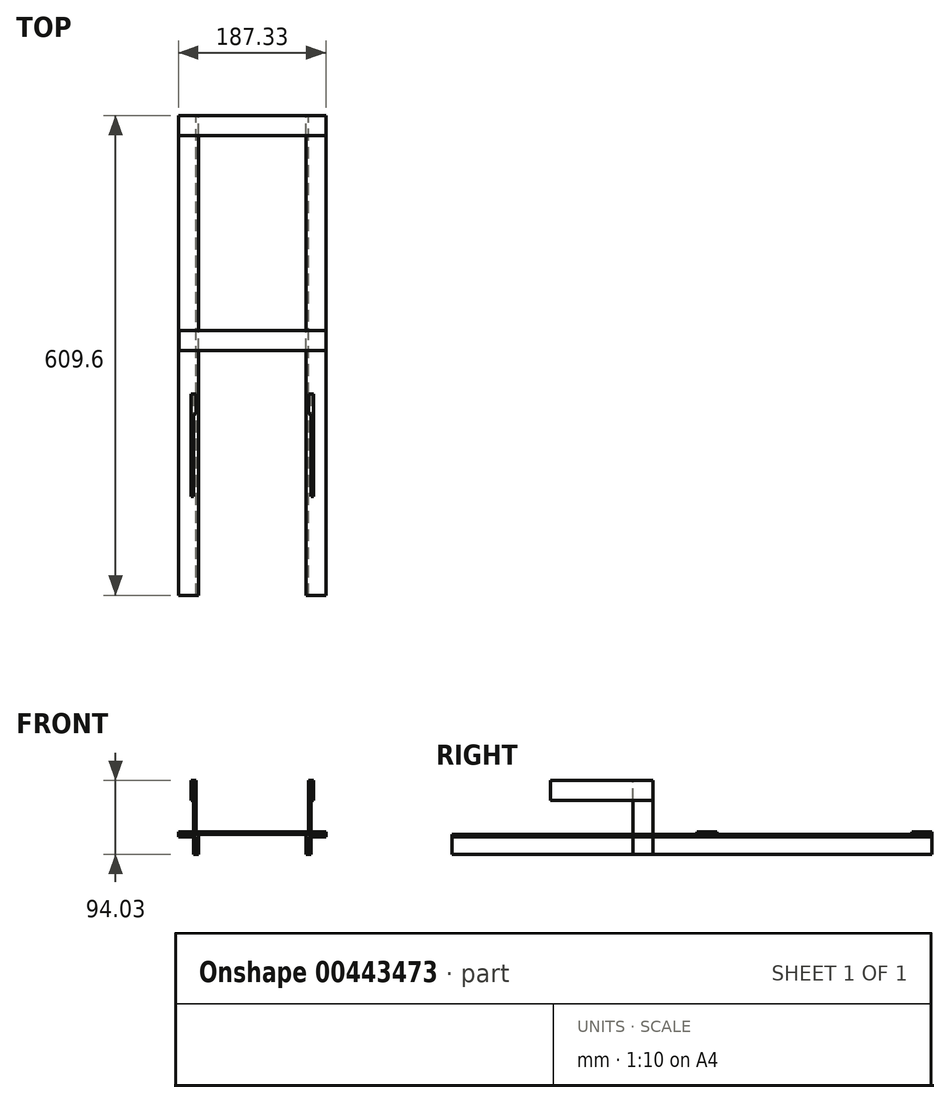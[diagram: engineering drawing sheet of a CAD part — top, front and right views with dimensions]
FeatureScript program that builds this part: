
annotation { "Feature Type Name" : "Feature", "Feature Type Description" : "" }
export const myFeature = defineFeature(function(context is Context, id is Id, definition is map)
    precondition{}
    {
        {
            var Q0;
            Q0=qCreatedBy(makeId("Front.planeOp"),FACE);
            var sketch = newSketch(context, id + "F0", { "sketchPlane" : qUnion([Q0])});
            skLineSegment(sketch, "E0", {"start": v(-20.3, 25.84) * mm, "end": v(5.1, 25.84) * mm});
            skLineSegment(sketch, "E1", {"start": v(5.1, 25.84) * mm, "end": v(5.1, 0.44) * mm});
            skLineSegment(sketch, "E2.0", {"start": v(1.93, 22.66) * mm, "end": v(1.93, 11.04) * mm});
            skLineSegment(sketch, "E2.1", {"start": v(-20.3, 22.66) * mm, "end": v(1.93, 22.66) * mm});
            skLineSegment(sketch, "E3", {"start": v(-20.3, 25.84) * mm, "end": v(-20.3, 22.66) * mm});
            skLineSegment(sketch, "E4", {"start": v(5.1, 0.44) * mm, "end": v(1.93, 0.44) * mm});
            skLineSegment(sketch, "E5", {"start": v(1.93, 11.04) * mm, "end": v(1.93, 0.44) * mm});
            skPoint(sketch, "E6.orphan", {"position": v(0, 0.44) * mm});
            skSolve(sketch);
        }
        {
            var Q0;
            Q0 = qSketchRegion(id + "F0", true);
            extrude(context, id + "F1", {"entities" : qUnion([Q0]), "depth" : 609.6 * mm});
        }
        {
            var Q0;
            Q0=makeQuery(id+"F1.opExtrude","SWEPT_FACE",FACE,{"disambiguationData":[OSD([sQuery(id+"F0.wireOp",EDGE,"E0")])]});
            var sketch = newSketch(context, id + "F2", { "sketchPlane" : qUnion([Q0])});
            skLineSegment(sketch, "E7.bottom", {"start": v(-20.3, 0) * mm, "end": v(167.03, 0) * mm});
            skLineSegment(sketch, "E7.top", {"start": v(-20.3, -25.4) * mm, "end": v(167.03, -25.4) * mm});
            skLineSegment(sketch, "E7.left", {"start": v(-20.3, 0) * mm, "end": v(-20.3, -25.4) * mm});
            skLineSegment(sketch, "E7.right", {"start": v(167.03, 0) * mm, "end": v(167.03, -25.4) * mm});
            skSolve(sketch);
        }
        {
            var Q0;
            {var subQ3=sQuery(id+"F2.wireOp",EDGE,"E7.right");Q0=makeQuery(id+"F2.imprint","IMPRINT",FACE,{"disambiguationData":[TD([[makeQuery(id+"F2.imprint","IMPRINT",EDGE,{"derivedFrom":subQ3}),-1.0]])]});}
            var Q1;
            {var subQ0=sQuery(id+"F2.wireOp",EDGE,"E7.left");Q1=makeQuery(id+"F2.imprint","IMPRINT",FACE,{"disambiguationData":[TD([[makeQuery(id+"F2.imprint","IMPRINT",EDGE,{"derivedFrom":subQ0}),-1.0]])]});}
            extrude(context, id + "F3", {"entities" : qUnion([Q0, Q1]), "operationType" : NewBodyOperationType.ADD, "depth" : 3.17 * mm});
        }
        {
            var Q0;
            Q0=makeQuery(id+"F3.boolean.opBoolean","MERGE",FACE,{"derivedFrom":[makeQuery(id+"F1.opExtrude","CAP_FACE",FACE,{"disambiguationData":[OSD([sQuery(id+"F0.wireOp",EDGE,"E0"),sQuery(id+"F0.wireOp",EDGE,"E1"),sQuery(id+"F0.wireOp",EDGE,"E2.0"),sQuery(id+"F0.wireOp",EDGE,"E2.1"),sQuery(id+"F0.wireOp",EDGE,"E3"),sQuery(id+"F0.wireOp",EDGE,"E4"),sQuery(id+"F0.wireOp",EDGE,"E5")])],"isStart":true}),makeQuery(id+"F3.opExtrude","SWEPT_FACE",FACE,{"disambiguationData":[OSD([sQuery(id+"F2.wireOp",EDGE,"E7.bottom")])]})]});
            var sketch = newSketch(context, id + "F4", { "sketchPlane" : qUnion([Q0])});
            skLineSegment(sketch, "E8", {"start": v(-167.03, 25.84) * mm, "end": v(-141.63, 25.84) * mm});
            skLineSegment(sketch, "E9", {"start": v(-141.63, 25.84) * mm, "end": v(-141.63, 0.44) * mm});
            skLineSegment(sketch, "E10", {"start": v(-167.03, 25.84) * mm, "end": v(-167.03, 22.66) * mm});
            skLineSegment(sketch, "E11", {"start": v(-167.03, 22.66) * mm, "end": v(-144.8, 22.66) * mm});
            skLineSegment(sketch, "E12", {"start": v(-144.8, 22.66) * mm, "end": v(-144.8, 0.44) * mm});
            skPoint(sketch, "E13.end.orphan", {"position": v(-144.8, 0.44) * mm});
            skPoint(sketch, "E14.orphan", {"position": v(-144.8, 0) * mm});
            skLineSegment(sketch, "E15", {"start": v(-141.63, 0.44) * mm, "end": v(-144.8, 0.44) * mm});
            skSolve(sketch);
        }
        {
            var Q0;
            Q0=makeQuery(id+"F4.imprint","IMPRINT",FACE,{"disambiguationData":[TD([[makeQuery(id+"F4.imprint","IMPRINT",EDGE,{"derivedFrom":sQuery(id+"F4.wireOp",EDGE,"E8")}),1.0]])]});
            extrude(context, id + "F5", {"entities" : qUnion([Q0]), "depth" : -609.6 * mm});
        }
        {
            var Q0;
            Q0=makeQuery(id+"F5.opExtrude","SWEPT_FACE",FACE,{"disambiguationData":[OSD([sQuery(id+"F4.wireOp",EDGE,"E8")])]});
            var sketch = newSketch(context, id + "F6", { "sketchPlane" : qUnion([Q0])});
            skLineSegment(sketch, "E16", {"start": v(141.63, 0) * mm, "end": v(141.63, -298.45) * mm});
            skLineSegment(sketch, "E17.bottom", {"start": v(167.03, -298.45) * mm, "end": v(-19.32, -298.45) * mm});
            skLineSegment(sketch, "E17.top", {"start": v(167.03, -273.05) * mm, "end": v(-19.32, -273.05) * mm});
            skLineSegment(sketch, "E17.left", {"start": v(167.03, -298.45) * mm, "end": v(167.03, -273.05) * mm});
            skLineSegment(sketch, "E17.right", {"start": v(-19.32, -298.45) * mm, "end": v(-19.32, -273.05) * mm});
            skSolve(sketch);
        }
        {
            var Q0;
            Q0 = qSketchRegion(id + "F6", true);
            extrude(context, id + "F7", {"entities" : qUnion([Q0]), "depth" : 3.17 * mm});
        }
        {
            var Q0;
            Q0=makeQuery(id+"F5.opExtrude","SWEPT_FACE",FACE,{"disambiguationData":[OSD([sQuery(id+"F4.wireOp",EDGE,"E12")])]});
            var sketch = newSketch(context, id + "F8", { "sketchPlane" : qUnion([Q0])});
            skLineSegment(sketch, "E18.bottom", {"start": v(-353.92, 0.44) * mm, "end": v(-379.32, 0.44) * mm});
            skLineSegment(sketch, "E18.top", {"start": v(-353.92, 94.47) * mm, "end": v(-379.32, 94.47) * mm});
            skLineSegment(sketch, "E18.left", {"start": v(-353.92, 0.44) * mm, "end": v(-353.92, 94.47) * mm});
            skLineSegment(sketch, "E18.right", {"start": v(-379.32, 0.44) * mm, "end": v(-379.32, 94.47) * mm});
            skLineSegment(sketch, "E19", {"start": v(-300.04, 22.66) * mm, "end": v(-353.92, 22.66) * mm});
            skSolve(sketch);
        }
        {
            var Q0;
            Q0 = qSketchRegion(id + "F8", true);
            extrude(context, id + "F9", {"entities" : qUnion([Q0]), "operationType" : NewBodyOperationType.ADD, "depth" : 3.17 * mm});
        }
        {
            var Q0;
            {var subQ0=sQuery(id+"F8.wireOp",EDGE,"E18.left");var subQ1=sQuery(id+"F8.wireOp",EDGE,"E18.top");var subQ2=sQuery(id+"F8.wireOp",EDGE,"E18.right");Q0=makeQuery(id+"F9.boolean.opBoolean","SPLIT",FACE,{"disambiguationData":[TD([makeQuery(id+"F5.opExtrude","SWEPT_FACE",FACE,{"disambiguationData":[OSD([sQuery(id+"F4.wireOp",EDGE,"E8")])]})])],"derivedFrom":makeQuery(id+"F9.opExtrude","CAP_FACE",FACE,{"disambiguationData":[OSD([sQuery(id+"F8.wireOp",EDGE,"E18.bottom"),subQ1,subQ0,subQ2])],"isStart":false})});}
            var sketch = newSketch(context, id + "F10", { "sketchPlane" : qUnion([Q0])});
            skLineSegment(sketch, "E20.bottom", {"start": v(-353.92, 94.47) * mm, "end": v(-484.1, 94.47) * mm});
            skLineSegment(sketch, "E20.top", {"start": v(-353.92, 69.07) * mm, "end": v(-484.1, 69.07) * mm});
            skLineSegment(sketch, "E20.left", {"start": v(-353.92, 94.47) * mm, "end": v(-353.92, 69.07) * mm});
            skLineSegment(sketch, "E20.right", {"start": v(-484.1, 94.47) * mm, "end": v(-484.1, 69.07) * mm});
            skSolve(sketch);
        }
        {
            var Q0;
            Q0 = qSketchRegion(id + "F10", true);
            extrude(context, id + "F11", {"entities" : qUnion([Q0]), "operationType" : NewBodyOperationType.ADD, "depth" : 3.17 * mm});
        }
        {
            var Q0;
            Q0=makeQuery(id+"F1.opExtrude","SWEPT_FACE",FACE,{"disambiguationData":[OSD([sQuery(id+"F0.wireOp",EDGE,"E2.0"),sQuery(id+"F0.wireOp",EDGE,"E5")])]});
            var sketch = newSketch(context, id + "F12", { "sketchPlane" : qUnion([Q0])});
            skLineSegment(sketch, "E21.bottom", {"start": v(354.04, 0.44) * mm, "end": v(379.44, 0.44) * mm});
            skLineSegment(sketch, "E21.top", {"start": v(354.04, 94.47) * mm, "end": v(379.44, 94.47) * mm});
            skLineSegment(sketch, "E21.left", {"start": v(354.04, 0.44) * mm, "end": v(354.04, 94.47) * mm});
            skLineSegment(sketch, "E21.right", {"start": v(379.44, 0.44) * mm, "end": v(379.44, 94.47) * mm});
            skSolve(sketch);
        }
        {
            var Q0;
            Q0 = qSketchRegion(id + "F12", true);
            extrude(context, id + "F13", {"entities" : qUnion([Q0]), "operationType" : NewBodyOperationType.ADD, "depth" : 3.17 * mm});
        }
        {
            var Q0;
            {var subQ0=sQuery(id+"F12.wireOp",EDGE,"E21.left");var subQ1=sQuery(id+"F12.wireOp",EDGE,"E21.top");var subQ2=sQuery(id+"F12.wireOp",EDGE,"E21.right");Q0=makeQuery(id+"F13.boolean.opBoolean","SPLIT",FACE,{"disambiguationData":[TD([makeQuery(id+"F1.opExtrude","SWEPT_FACE",FACE,{"disambiguationData":[OSD([sQuery(id+"F0.wireOp",EDGE,"E0")])]})])],"derivedFrom":makeQuery(id+"F13.opExtrude","CAP_FACE",FACE,{"disambiguationData":[OSD([sQuery(id+"F12.wireOp",EDGE,"E21.bottom"),subQ1,subQ0,subQ2])],"isStart":false})});}
            var sketch = newSketch(context, id + "F14", { "sketchPlane" : qUnion([Q0])});
            skLineSegment(sketch, "E22.bottom", {"start": v(354.04, 94.47) * mm, "end": v(484.22, 94.47) * mm});
            skLineSegment(sketch, "E22.top", {"start": v(354.04, 69.07) * mm, "end": v(484.22, 69.07) * mm});
            skLineSegment(sketch, "E22.left", {"start": v(354.04, 94.47) * mm, "end": v(354.04, 69.07) * mm});
            skLineSegment(sketch, "E22.right", {"start": v(484.22, 94.47) * mm, "end": v(484.22, 69.07) * mm});
            skSolve(sketch);
        }
        {
            var Q0;
            Q0 = qSketchRegion(id + "F14", true);
            extrude(context, id + "F15", {"entities" : qUnion([Q0]), "operationType" : NewBodyOperationType.ADD, "depth" : 3.17 * mm});
        }
    });
